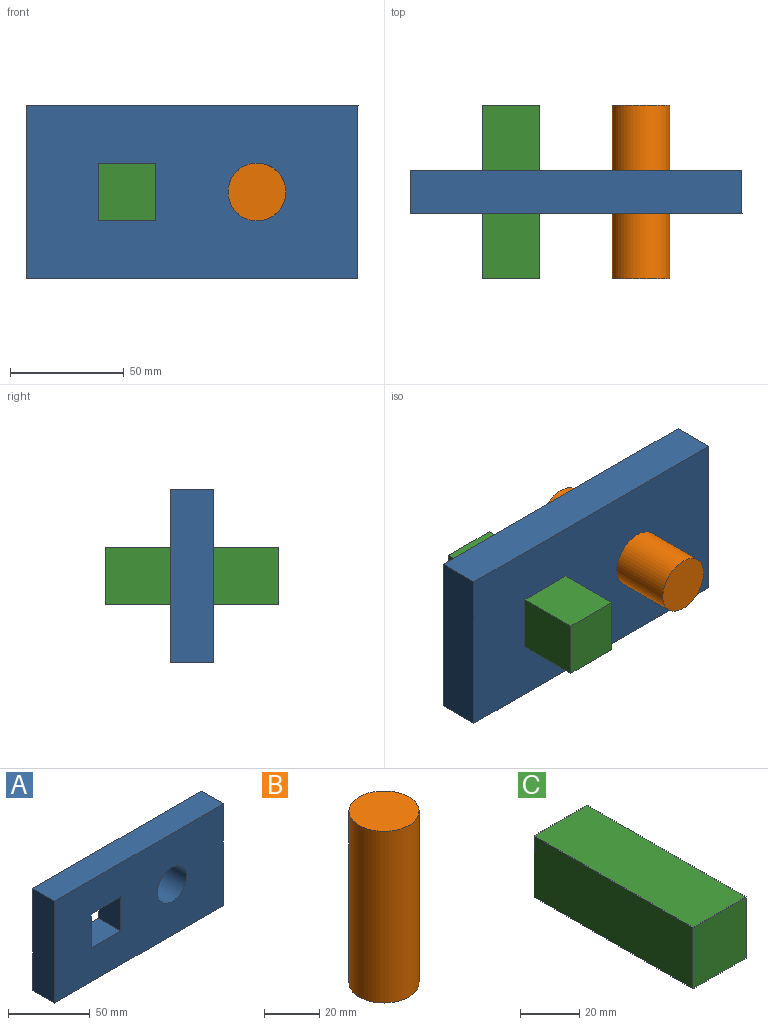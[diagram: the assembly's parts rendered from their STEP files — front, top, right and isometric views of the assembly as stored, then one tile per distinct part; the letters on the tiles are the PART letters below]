
ASSEMBLY  parts=3 mates=2
PART A: 11 faces, bbox 146.1x19.1x76.2 mm
  f0: plane 146.05x76.2mm, normal (0,-1,0), area 9977.1mm2, adj f2,f3,f4,f5,f6,f7,f8,f9
  f1: plane 146.05x76.2mm, normal (0,1,0), area 9977.1mm2, adj f2,f3,f4,f5,f6,f7,f8,f9
  f2: plane 76.2x19.05mm, normal (-1,0,0), area 1451.6mm2, adj f0,f1,f4,f5
  f3: plane 76.2x19.05mm, normal (1,0,0), area 1451.6mm2, adj f0,f1,f4,f5
  f4: plane 146.05x19.05mm, normal (0,0,1), area 2782.3mm2, adj f0,f1,f2,f3
  f5: plane 146.05x19.05mm, normal (0,0,-1), area 2782.3mm2, adj f0,f1,f2,f3
  f6: cylinder r=12.7mm len=25.4mm, axis (0,-1,0), area 1520.1mm2, adj f0,f1
  f7: plane 25.4x19.05mm, normal (1,0,0), area 483.9mm2, adj f0,f1,f8,f10
  f8: plane 25.4x19.05mm, normal (0,0,1), area 483.9mm2, adj f0,f1,f7,f9
  f9: plane 25.4x19.05mm, normal (-1,0,0), area 483.9mm2, adj f0,f1,f8,f10
  f10: plane 25.4x19.05mm, normal (0,0,-1), area 483.9mm2, adj f0,f1,f7,f9
PART B: 3 faces, bbox 25.4x25.4x76.2 mm
  f0: cylinder r=12.7mm len=76.2mm, axis (0,0,-1), area 6080.5mm2, adj f1,f2
  f1: plane 25.4x25.4mm, normal (0,0,1), area 506.7mm2, adj f0
  f2: plane 25.4x25.4mm, normal (0,0,-1), area 506.7mm2, adj f0
PART C: 6 faces, bbox 25.4x76.2x25.4 mm
  f0: plane 76.2x25.4mm, normal (-1,0,0), area 1935.5mm2, adj f1,f3,f4,f5
  f1: plane 76.2x25.4mm, normal (0,0,-1), area 1935.5mm2, adj f0,f2,f4,f5
  f2: plane 76.2x25.4mm, normal (1,0,0), area 1935.5mm2, adj f1,f3,f4,f5
  f3: plane 76.2x25.4mm, normal (0,0,1), area 1935.5mm2, adj f0,f2,f4,f5
  f4: plane 25.4x25.4mm, normal (0,-1,0), area 645.2mm2, adj f0,f1,f2,f3
  f5: plane 25.4x25.4mm, normal (0,1,0), area 645.2mm2, adj f0,f1,f2,f3
PLACE A rot(axis=(0.31,0.93,0.18),0deg) t=(82.34,-41.34,24.81)mm
PLACE B rot(axis=(-1,0,0),90deg) t=(113.79,-82,62.91)mm
PLACE C rot(axis=(0.31,0.93,0.18),0deg) t=(66.17,-5.8,50.21)mm
MATE fastened B.f0 <-> A.f6  axis (0,-1,0) through (113.79,-43.9,62.91)mm
MATE fastened C.f3 <-> A.f10  axis (0,0,1) through (56.64,-43.9,75.61)mm
